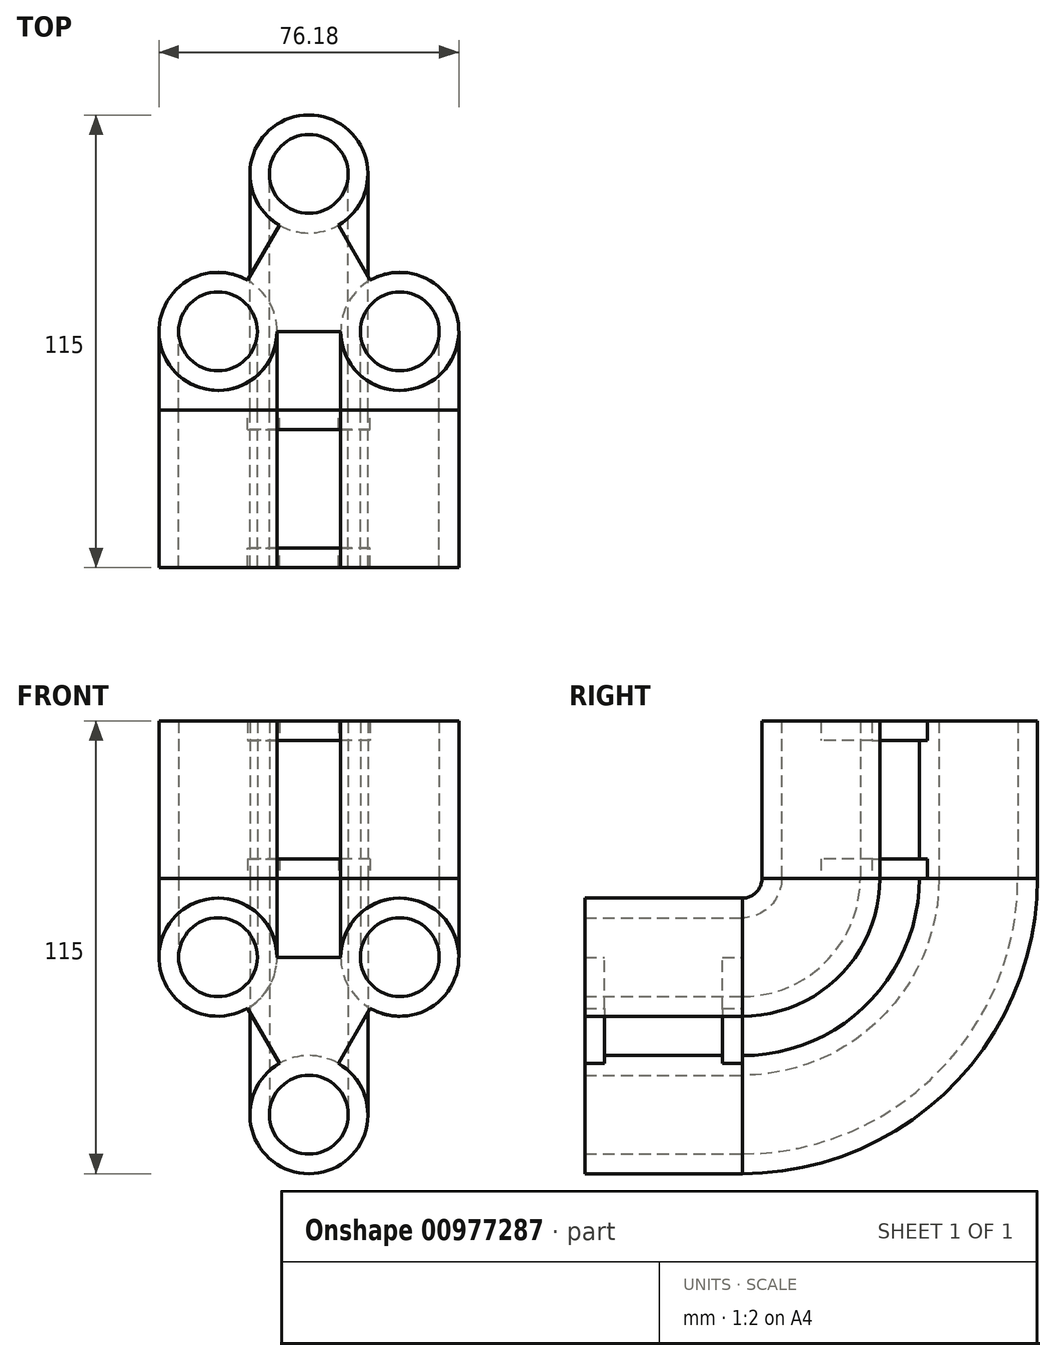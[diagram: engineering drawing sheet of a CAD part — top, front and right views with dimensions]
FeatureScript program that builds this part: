
annotation { "Feature Type Name" : "Feature", "Feature Type Description" : "" }
export const myFeature = defineFeature(function(context is Context, id is Id, definition is map)
    precondition{}
    {
        {
            var Q0;
            Q0=qCreatedBy(makeId("Front.planeOp"),FACE);
            var sketch = newSketch(context, id + "F0", { "sketchPlane" : qUnion([Q0])});
            skCircle(sketch, "E0", {"center": v(0, 0) * mm, "radius": 10 * mm});
            skCircle(sketch, "E1", {"center": v(23.1, 40) * mm, "radius": 10 * mm});
            skCircle(sketch, "E2", {"center": v(-23.1, 40) * mm, "radius": 10 * mm});
            skCircle(sketch, "E3", {"center": v(-23.1, 40) * mm, "radius": 15 * mm});
            skCircle(sketch, "E4", {"center": v(23.1, 40) * mm, "radius": 15 * mm});
            skCircle(sketch, "E5", {"center": v(0, 0) * mm, "radius": 15 * mm});
            skLineSegment(sketch, "E6", {"start": v(0, 0) * mm, "end": v(-23.1, 40) * mm});
            skLineSegment(sketch, "E7", {"start": v(23.1, 40) * mm, "end": v(0, 0) * mm});
            skLineSegment(sketch, "E8", {"start": v(-23.1, 40) * mm, "end": v(23.1, 40) * mm});
            skPoint(sketch, "E9", {"position": v(0, 40) * mm});
            skLineSegment(sketch, "E10", {"start": v(0, 65) * mm, "end": v(0, 65) * mm});
            skSolve(sketch);
        }
        {
            var Q0;
            Q0=qCreatedBy(makeId("Right.planeOp"),FACE);
            var sketch = newSketch(context, id + "F1", { "sketchPlane" : qUnion([Q0])});
            skArc(sketch, "E11", {"start": v(0, 40) * mm, "mid": v(14.14, 45.86) * mm, "end": v(20, 60) * mm});
            skLineSegment(sketch, "E12", {"start": v(20, 60) * mm, "end": v(0, 60) * mm});
            skLineSegment(sketch, "E13", {"start": v(0, 40) * mm, "end": v(0, 60) * mm});
            skSolve(sketch);
        }
        {
            var Q0;
            {var subQ0=sQuery(id+"F0.wireOp",EDGE,"E7");var subQ1=sQuery(id+"F0.wireOp",EDGE,"E1");var subQ2=makeQuery(id+"F0.imprint","INTERSECT",VERTEX,{"derivedFrom":[subQ1,subQ0]});Q0=makeQuery(id+"F0.imprint","IMPRINT",FACE,{"disambiguationData":[TD([[makeQuery(id+"F0.imprint","IMPRINT",EDGE,{"disambiguationData":[TD([[subQ2,-1.0]])],"derivedFrom":subQ1}),-1.0]])]});}
            var Q1;
            {var subQ0=sQuery(id+"F0.wireOp",EDGE,"E7");var subQ1=sQuery(id+"F0.wireOp",EDGE,"E1");var subQ2=makeQuery(id+"F0.imprint","INTERSECT",VERTEX,{"derivedFrom":[subQ1,subQ0]});Q1=makeQuery(id+"F0.imprint","IMPRINT",FACE,{"disambiguationData":[TD([[makeQuery(id+"F0.imprint","IMPRINT",EDGE,{"disambiguationData":[TD([[subQ2,1.0]])],"derivedFrom":subQ1}),-1.0]])]});}
            var Q2;
            {var subQ0=sQuery(id+"F0.wireOp",EDGE,"E6");var subQ1=sQuery(id+"F0.wireOp",EDGE,"E2");var subQ2=makeQuery(id+"F0.imprint","INTERSECT",VERTEX,{"derivedFrom":[subQ1,subQ0]});Q2=makeQuery(id+"F0.imprint","IMPRINT",FACE,{"disambiguationData":[TD([[makeQuery(id+"F0.imprint","IMPRINT",EDGE,{"disambiguationData":[TD([[subQ2,1.0]])],"derivedFrom":subQ1}),-1.0]])]});}
            var Q3;
            {var subQ0=sQuery(id+"F0.wireOp",EDGE,"E6");var subQ1=sQuery(id+"F0.wireOp",EDGE,"E2");var subQ2=makeQuery(id+"F0.imprint","INTERSECT",VERTEX,{"derivedFrom":[subQ1,subQ0]});Q3=makeQuery(id+"F0.imprint","IMPRINT",FACE,{"disambiguationData":[TD([[makeQuery(id+"F0.imprint","IMPRINT",EDGE,{"disambiguationData":[TD([[subQ2,-1.0]])],"derivedFrom":subQ1}),-1.0]])]});}
            var Q4;
            {var subQ0=sQuery(id+"F0.wireOp",EDGE,"E6");var subQ1=sQuery(id+"F0.wireOp",EDGE,"E0");var subQ2=makeQuery(id+"F0.imprint","INTERSECT",VERTEX,{"derivedFrom":[subQ1,subQ0]});Q4=makeQuery(id+"F0.imprint","IMPRINT",FACE,{"disambiguationData":[TD([[makeQuery(id+"F0.imprint","IMPRINT",EDGE,{"disambiguationData":[TD([[subQ2,-1.0]])],"derivedFrom":subQ1}),-1.0]])]});}
            var Q5;
            {var subQ0=sQuery(id+"F0.wireOp",EDGE,"E6");var subQ1=sQuery(id+"F0.wireOp",EDGE,"E0");var subQ2=makeQuery(id+"F0.imprint","INTERSECT",VERTEX,{"derivedFrom":[subQ1,subQ0]});Q5=makeQuery(id+"F0.imprint","IMPRINT",FACE,{"disambiguationData":[TD([[makeQuery(id+"F0.imprint","IMPRINT",EDGE,{"disambiguationData":[TD([[subQ2,1.0]])],"derivedFrom":subQ1}),-1.0]])]});}
            var Q6;
            Q6=sQuery(id+"F1.wireOp",EDGE,"E11");
            sweep(context, id + "F2", {"profiles" : qUnion([Q0, Q1, Q2, Q3, Q4, Q5]), "path" : qUnion([Q6])});
        }
        {
            var Q0;
            {var subQ0=sQuery(id+"F0.wireOp",EDGE,"E6");var subQ1=sQuery(id+"F0.wireOp",EDGE,"E2");var subQ2=makeQuery(id+"F0.imprint","INTERSECT",VERTEX,{"derivedFrom":[subQ1,subQ0]});Q0=makeQuery(id+"F0.imprint","IMPRINT",FACE,{"disambiguationData":[TD([[makeQuery(id+"F0.imprint","IMPRINT",EDGE,{"disambiguationData":[TD([[subQ2,1.0]])],"derivedFrom":subQ1}),-1.0]])]});}
            var Q1;
            {var subQ0=sQuery(id+"F0.wireOp",EDGE,"E6");var subQ1=sQuery(id+"F0.wireOp",EDGE,"E2");var subQ2=makeQuery(id+"F0.imprint","INTERSECT",VERTEX,{"derivedFrom":[subQ1,subQ0]});Q1=makeQuery(id+"F0.imprint","IMPRINT",FACE,{"disambiguationData":[TD([[makeQuery(id+"F0.imprint","IMPRINT",EDGE,{"disambiguationData":[TD([[subQ2,-1.0]])],"derivedFrom":subQ1}),-1.0]])]});}
            var Q2;
            {var subQ0=sQuery(id+"F0.wireOp",EDGE,"E6");var subQ1=sQuery(id+"F0.wireOp",EDGE,"E3");var subQ2=makeQuery(id+"F0.imprint","INTERSECT",VERTEX,{"derivedFrom":[subQ1,subQ0]});Q2=makeQuery(id+"F0.imprint","IMPRINT",FACE,{"disambiguationData":[TD([[makeQuery(id+"F0.imprint","IMPRINT",EDGE,{"disambiguationData":[TD([[subQ2,-1.0]])],"derivedFrom":subQ1}),-1.0]])]});}
            var Q3;
            {var subQ0=sQuery(id+"F0.wireOp",EDGE,"E7");var subQ1=sQuery(id+"F0.wireOp",EDGE,"E1");var subQ2=makeQuery(id+"F0.imprint","INTERSECT",VERTEX,{"derivedFrom":[subQ1,subQ0]});Q3=makeQuery(id+"F0.imprint","IMPRINT",FACE,{"disambiguationData":[TD([[makeQuery(id+"F0.imprint","IMPRINT",EDGE,{"disambiguationData":[TD([[subQ2,1.0]])],"derivedFrom":subQ1}),-1.0]])]});}
            var Q4;
            {var subQ0=sQuery(id+"F0.wireOp",EDGE,"E7");var subQ1=sQuery(id+"F0.wireOp",EDGE,"E1");var subQ2=makeQuery(id+"F0.imprint","INTERSECT",VERTEX,{"derivedFrom":[subQ1,subQ0]});Q4=makeQuery(id+"F0.imprint","IMPRINT",FACE,{"disambiguationData":[TD([[makeQuery(id+"F0.imprint","IMPRINT",EDGE,{"disambiguationData":[TD([[subQ2,-1.0]])],"derivedFrom":subQ1}),-1.0]])]});}
            var Q5;
            {var subQ0=sQuery(id+"F0.wireOp",EDGE,"E6");var subQ1=sQuery(id+"F0.wireOp",EDGE,"E0");var subQ2=makeQuery(id+"F0.imprint","INTERSECT",VERTEX,{"derivedFrom":[subQ1,subQ0]});Q5=makeQuery(id+"F0.imprint","IMPRINT",FACE,{"disambiguationData":[TD([[makeQuery(id+"F0.imprint","IMPRINT",EDGE,{"disambiguationData":[TD([[subQ2,1.0]])],"derivedFrom":subQ1}),-1.0]])]});}
            var Q6;
            {var subQ0=sQuery(id+"F0.wireOp",EDGE,"E6");var subQ1=sQuery(id+"F0.wireOp",EDGE,"E0");var subQ2=makeQuery(id+"F0.imprint","INTERSECT",VERTEX,{"derivedFrom":[subQ1,subQ0]});Q6=makeQuery(id+"F0.imprint","IMPRINT",FACE,{"disambiguationData":[TD([[makeQuery(id+"F0.imprint","IMPRINT",EDGE,{"disambiguationData":[TD([[subQ2,-1.0]])],"derivedFrom":subQ1}),-1.0]])]});}
            extrude(context, id + "F3", {"entities" : qUnion([Q0, Q1, Q2, Q3, Q4, Q5, Q6]), "depth" : 40 * mm, "offsetDistance" : 25 * mm});
        }
        {
            var Q0;
            {var subQ0=sQuery(id+"F0.wireOp",EDGE,"E6");var subQ1=sQuery(id+"F0.wireOp",EDGE,"E3");var subQ2=makeQuery(id+"F0.imprint","INTERSECT",VERTEX,{"derivedFrom":[subQ1,subQ0]});Q0=makeQuery(id+"F0.imprint","IMPRINT",FACE,{"disambiguationData":[TD([[makeQuery(id+"F0.imprint","IMPRINT",EDGE,{"disambiguationData":[TD([[subQ2,-1.0]])],"derivedFrom":subQ1}),-1.0]])]});}
            extrude(context, id + "F4", {"entities" : qUnion([Q0]), "operationType" : NewBodyOperationType.REMOVE, "depth" : 35 * mm, "offsetDistance" : 25 * mm, "hasSecondDirection" : true, "secondDirectionOppositeDirection" : false, "secondDirectionDepth" : 5 * mm});
        }
        {
            var Q0;
            Q0=makeQuery(id+"F2.opSweep","CAP_FACE",FACE,{"disambiguationData":[OSD([sQuery(id+"F0.wireOp",EDGE,"E3"),sQuery(id+"F1.wireOp",VERTEX,"E11.end")])],"isStart":false});
            var sketch = newSketch(context, id + "F5", { "sketchPlane" : qUnion([Q0])});
            skCircle(sketch, "E14", {"center": v(-23.1, 20) * mm, "radius": 15 * mm});
            skCircle(sketch, "E15", {"center": v(23.1, 20) * mm, "radius": 15 * mm});
            skCircle(sketch, "E16", {"center": v(0, 60) * mm, "radius": 15 * mm});
            skLineSegment(sketch, "E17", {"start": v(-23.1, 20) * mm, "end": v(23.1, 20) * mm});
            skLineSegment(sketch, "E18", {"start": v(23.1, 20) * mm, "end": v(0, 60) * mm});
            skLineSegment(sketch, "E19", {"start": v(0, 60) * mm, "end": v(-23.1, 20) * mm});
            skCircle(sketch, "E20", {"center": v(-23.1, 20) * mm, "radius": 10 * mm});
            skCircle(sketch, "E21", {"center": v(0, 60) * mm, "radius": 10 * mm});
            skCircle(sketch, "E22", {"center": v(23.1, 20) * mm, "radius": 10 * mm});
            skSolve(sketch);
        }
        {
            var Q0;
            Q0=qSketchRegion(id+"F5",true);
            extrude(context, id + "F6", {"entities" : qUnion([Q0]), "depth" : 40 * mm, "offsetDistance" : 25 * mm});
        }
        {
            var Q0;
            Q0=qSketchRegion(id+"F5",true);
            extrude(context, id + "F7", {"entities" : qUnion([Q0]), "depth" : 40 * mm, "offsetDistance" : 25 * mm});
        }
        {
            var Q0;
            {var subQ0=sQuery(id+"F5.wireOp",EDGE,"E17");var subQ1=sQuery(id+"F5.wireOp",EDGE,"E14");var subQ2=makeQuery(id+"F5.imprint","INTERSECT",VERTEX,{"derivedFrom":[subQ1,subQ0]});Q0=makeQuery(id+"F5.imprint","IMPRINT",FACE,{"disambiguationData":[TD([[makeQuery(id+"F5.imprint","IMPRINT",EDGE,{"disambiguationData":[TD([[subQ2,1.0]])],"derivedFrom":subQ1}),1.0]])]});}
            extrude(context, id + "F8", {"entities" : qUnion([Q0]), "operationType" : NewBodyOperationType.REMOVE, "depth" : 35 * mm, "offsetDistance" : 25 * mm, "hasSecondDirection" : true, "secondDirectionOppositeDirection" : false, "secondDirectionDepth" : 5 * mm});
        }
    });
